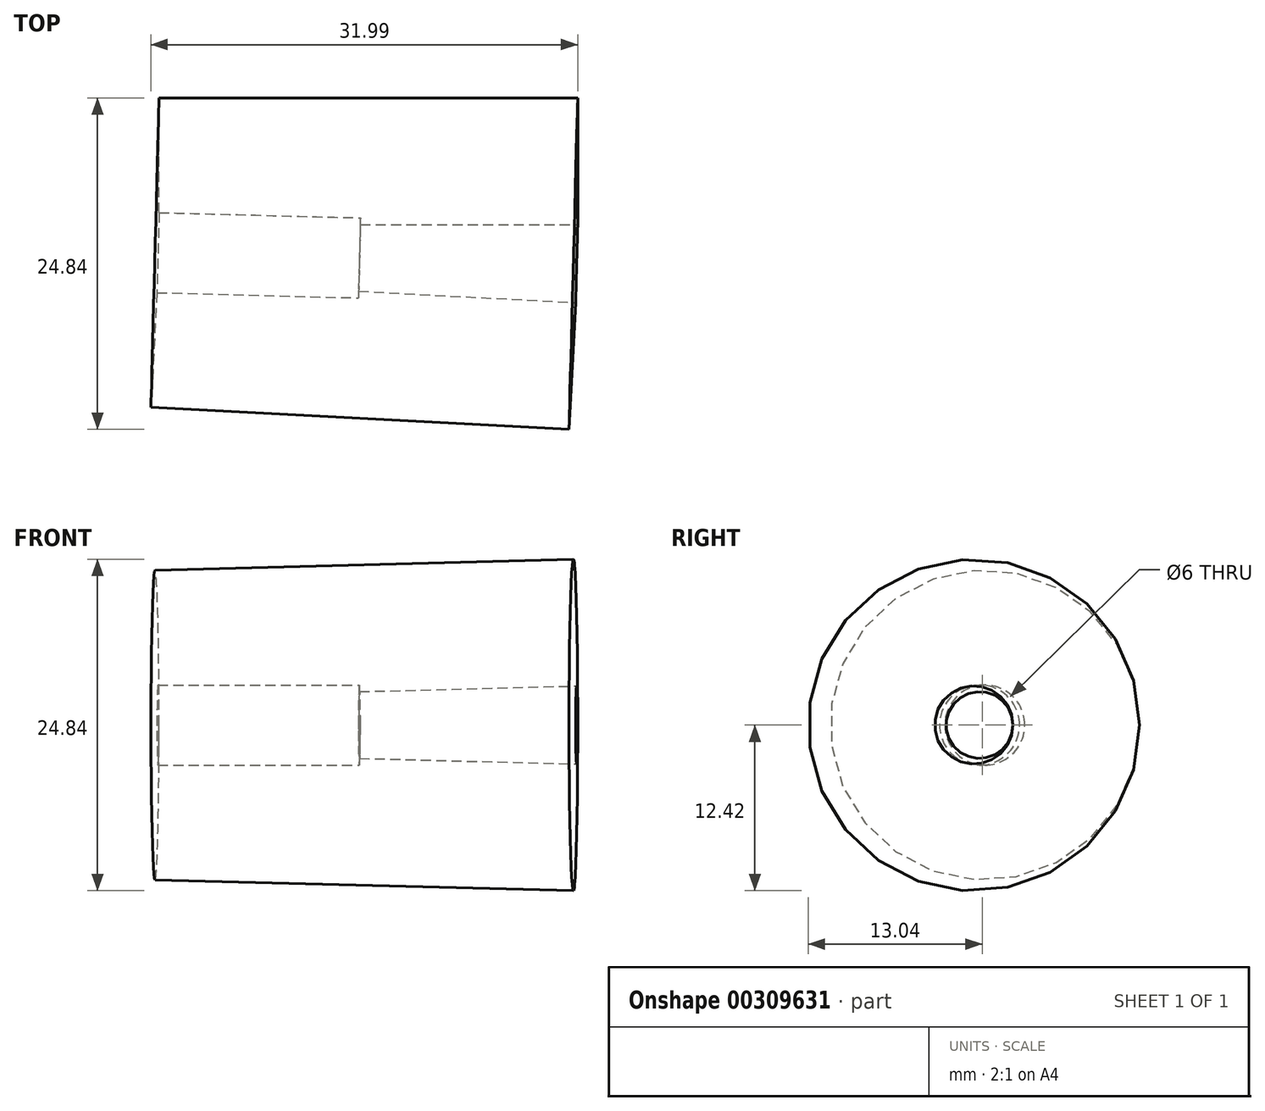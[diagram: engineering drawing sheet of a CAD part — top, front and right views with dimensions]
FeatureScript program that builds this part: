
annotation { "Feature Type Name" : "Feature", "Feature Type Description" : "" }
export const myFeature = defineFeature(function(context is Context, id is Id, definition is map)
    precondition{}
    {
        {
            var Q0;
            Q0=qCreatedBy(makeId("Top.planeOp"),FACE);
            var sketch = newSketch(context, id + "F0", { "sketchPlane" : qUnion([Q0])});
            skLineSegment(sketch, "E0", {"start": v(0, 0) * mm, "end": v(16.3, 0) * mm, "construction": true});
            skPoint(sketch, "E1.start.orphan", {"position": v(5.29, 4.35) * mm});
            skLineSegment(sketch, "E2", {"start": v(0, 2.5) * mm, "end": v(16.3, 2.5) * mm});
            skLineSegment(sketch, "E3", {"start": v(16.3, 2.5) * mm, "end": v(16.3, 12) * mm});
            skLineSegment(sketch, "E4", {"start": v(16.3, 12) * mm, "end": v(0, 12) * mm});
            skLineSegment(sketch, "E5", {"start": v(0, 12) * mm, "end": v(0, 2.5) * mm});
            skLineSegment(sketch, "E6", {"start": v(0, 12) * mm, "end": v(-15.1, 12) * mm});
            skLineSegment(sketch, "E7", {"start": v(-15.1, 12) * mm, "end": v(-15.1, 3.4) * mm});
            skPoint(sketch, "E8.end.orphan", {"position": v(-15.1, -2.27) * mm});
            skPoint(sketch, "E9.start.orphan", {"position": v(-6.1, 0.65) * mm});
            skPoint(sketch, "E10.end.orphan", {"position": v(-1.2, -0.4) * mm});
            skPoint(sketch, "E10.start.orphan", {"position": v(-0.4, 2.5) * mm});
            skLineSegment(sketch, "E11", {"start": v(0, 0) * mm, "end": v(-13.9, 0.36) * mm, "construction": true});
            skLineSegment(sketch, "E12", {"start": v(-12.45, 0.33) * mm, "end": v(-12.37, 3.33) * mm});
            skLineSegment(sketch, "E13", {"start": v(-12.37, 3.33) * mm, "end": v(0, 3) * mm});
            skLineSegment(sketch, "E14", {"start": v(-12.37, 3.33) * mm, "end": v(-15.1, 3.4) * mm});
            skPoint(sketch, "E15.end.orphan", {"position": v(16.3, -12) * mm});
            skSolve(sketch);
        }
        {
            var Q0;
            {var subQ1=sQuery(id+"F0.wireOp",EDGE,"E6");Q0=makeQuery(id+"F0.imprint","IMPRINT",FACE,{"disambiguationData":[TD([[makeQuery(id+"F0.imprint","IMPRINT",EDGE,{"derivedFrom":subQ1}),1.0]])]});}
            var Q1;
            {var subQ3=sQuery(id+"F0.wireOp",EDGE,"E2");Q1=makeQuery(id+"F0.imprint","IMPRINT",FACE,{"disambiguationData":[TD([[makeQuery(id+"F0.imprint","IMPRINT",EDGE,{"derivedFrom":subQ3}),1.0]])]});}
            var Q2;
            Q2=sQuery(id+"F0.wireOp",EDGE,"E11");
            revolve(context, id + "F1", {"entities" : qUnion([Q0, Q1]), "axis" : qUnion([Q2]), "revolveType" : RevolveType.FULL});
        }
    });
